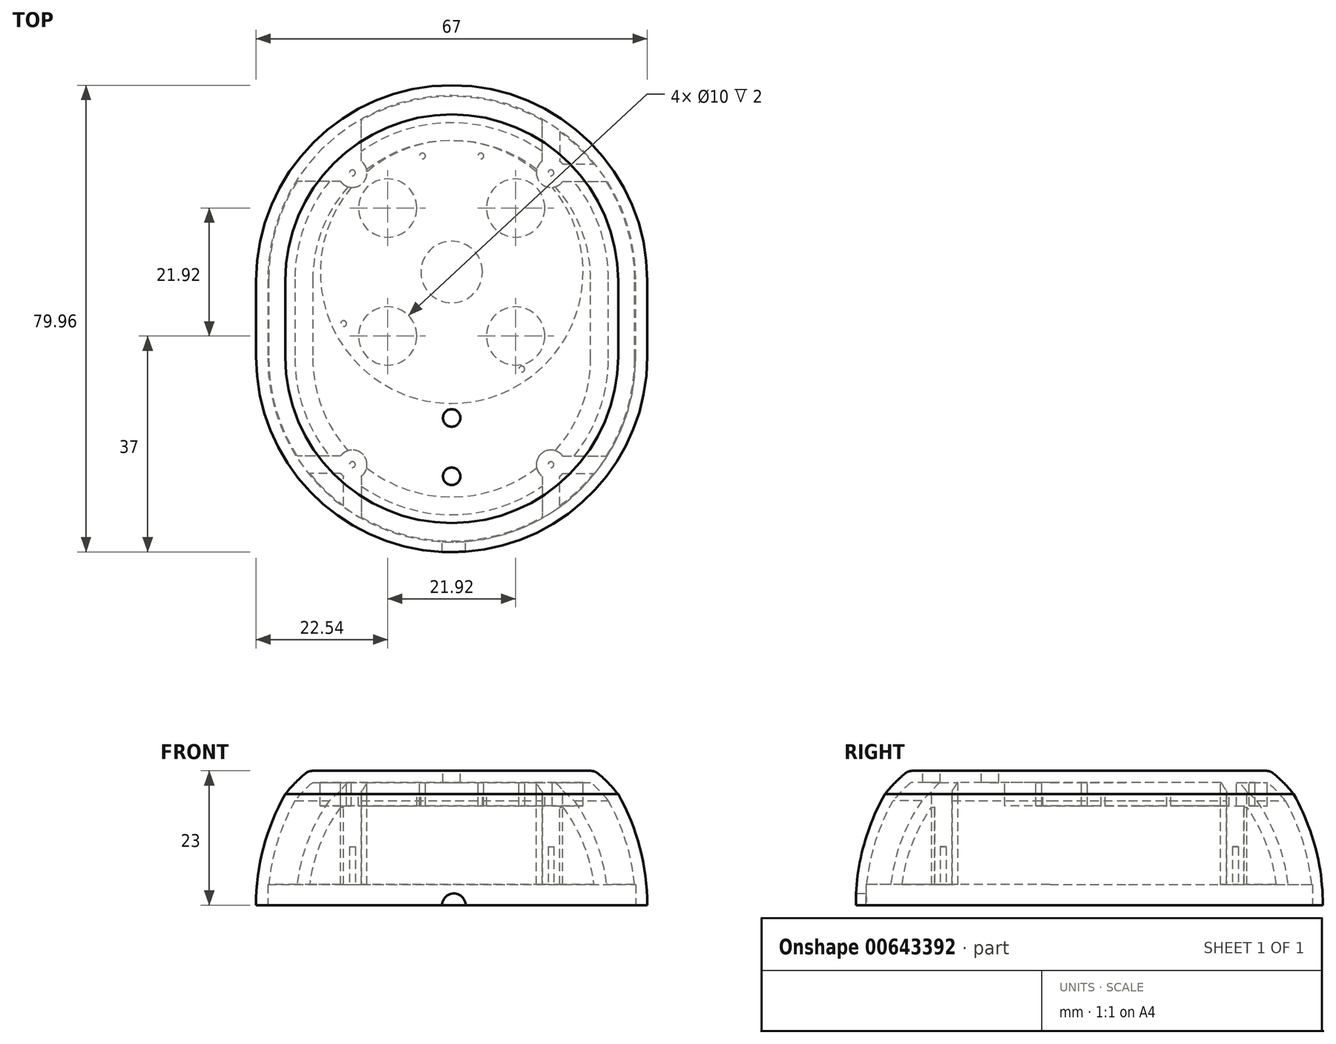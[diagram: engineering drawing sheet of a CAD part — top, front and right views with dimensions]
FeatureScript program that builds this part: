
annotation { "Feature Type Name" : "Feature", "Feature Type Description" : "" }
export const myFeature = defineFeature(function(context is Context, id is Id, definition is map)
    precondition{}
    {
        {
            var Q0;
            Q0=qCreatedBy(makeId("Front.planeOp"),FACE);
            var sketch = newSketch(context, id + "F0", { "sketchPlane" : qUnion([Q0])});
            skLineSegment(sketch, "E0", {"start": v(0, 0) * mm, "end": v(33.5, 0) * mm});
            skLineSegment(sketch, "E1", {"start": v(33.5, 0) * mm, "end": v(33.5, 19) * mm});
            skLineSegment(sketch, "E2", {"start": v(33.5, 19) * mm, "end": v(28.5, 19) * mm});
            skArc(sketch, "E3", {"start": v(33.5, 0) * mm, "mid": v(32.23, 9.82) * mm, "end": v(28.5, 19) * mm});
            skLineSegment(sketch, "E4", {"start": v(28.5, 19) * mm, "end": v(28.5, 23) * mm});
            skLineSegment(sketch, "E5", {"start": v(28.5, 23) * mm, "end": v(24.5, 23) * mm});
            skArc(sketch, "E6", {"start": v(28.5, 19) * mm, "mid": v(26.62, 21.12) * mm, "end": v(24.5, 23) * mm});
            skLineSegment(sketch, "E7", {"start": v(0, 25) * mm, "end": v(0, 0) * mm});
            skLineSegment(sketch, "E8", {"start": v(24.5, 23) * mm, "end": v(0, 23) * mm});
            skLineSegment(sketch, "E9.0", {"start": v(23.8, 21) * mm, "end": v(0, 21) * mm});
            skArc(sketch, "E9.1", {"start": v(26.83, 17.88) * mm, "mid": v(25.4, 19.52) * mm, "end": v(23.8, 21) * mm});
            skArc(sketch, "E9.2", {"start": v(31.5, 0) * mm, "mid": v(30.31, 9.24) * mm, "end": v(26.83, 17.88) * mm});
            skLineSegment(sketch, "E10", {"start": v(0, 23) * mm, "end": v(0, 32.6) * mm});
            skLineSegment(sketch, "E11", {"start": v(0, 32.6) * mm, "end": v(44.3, 32.6) * mm});
            skLineSegment(sketch, "E12", {"start": v(44.3, 32.6) * mm, "end": v(44.3, 0) * mm});
            skLineSegment(sketch, "E13", {"start": v(44.3, 0) * mm, "end": v(33.5, 0) * mm});
            skSolve(sketch);
        }
        {
            var Q0;
            {var subQ3=sQuery(id+"F0.wireOp",EDGE,"E3");Q0=makeQuery(id+"F0.imprint","IMPRINT",FACE,{"disambiguationData":[TD([[makeQuery(id+"F0.imprint","IMPRINT",EDGE,{"derivedFrom":subQ3}),1.0]])]});}
            var Q1;
            {var subQ0=sQuery(id+"F0.wireOp",EDGE,"E9.0");Q1=makeQuery(id+"F0.imprint","IMPRINT",FACE,{"disambiguationData":[TD([[makeQuery(id+"F0.imprint","IMPRINT",EDGE,{"derivedFrom":subQ0}),1.0]])]});}
            extrude(context, id + "F1", {"entities" : qUnion([Q0, Q1]), "depth" : (80 / 2 - 67 / 2) * mm, "offsetDistance" : 25 * mm});
        }
        {
            var Q0;
            Q0=makeQuery(id+"F1.opExtrude","CAP_FACE",FACE,{"disambiguationData":[OSD([sQuery(id+"F0.wireOp",EDGE,"E0"),sQuery(id+"F0.wireOp",EDGE,"E3"),sQuery(id+"F0.wireOp",EDGE,"E6"),sQuery(id+"F0.wireOp",EDGE,"E7"),sQuery(id+"F0.wireOp",EDGE,"E8")])],"isStart":false});
            var Q1;
            Q1=makeQuery(id+"F1.opExtrude","CAP_EDGE",EDGE,{"disambiguationData":[OSD([sQuery(id+"F0.wireOp",EDGE,"E7")])],"isStart":false});
            revolve(context, id + "F2", {"operationType" : NewBodyOperationType.ADD, "entities" : qUnion([Q0]), "axis" : qUnion([Q1]), "revolveType" : RevolveType.ONE_DIRECTION, "angle" : 180 * degree});
        }
        {
            var Q0;
            Q0=makeQuery(id+"F2.opRevolve","CAP_FACE",FACE,{"disambiguationData":[OSD([sQuery(id+"F0.wireOp",EDGE,"E0"),sQuery(id+"F0.wireOp",EDGE,"E3"),sQuery(id+"F0.wireOp",EDGE,"E6"),sQuery(id+"F0.wireOp",EDGE,"E7"),sQuery(id+"F0.wireOp",EDGE,"E8")])],"isStart":true});
            extrude(context, id + "F3", {"entities" : qUnion([Q0]), "operationType" : NewBodyOperationType.ADD, "depth" : (80 / 2 - 67 / 2) * mm, "offsetDistance" : 25 * mm});
        }
        {
            var Q0;
            {var subQ0=sQuery(id+"F0.wireOp",EDGE,"E9.0");Q0=makeQuery(id+"F0.imprint","IMPRINT",FACE,{"disambiguationData":[TD([[makeQuery(id+"F0.imprint","IMPRINT",EDGE,{"derivedFrom":subQ0}),1.0]])]});}
            extrude(context, id + "F4", {"entities" : qUnion([Q0]), "operationType" : NewBodyOperationType.REMOVE, "depth" : (81.5 / 2 - 68 / 2) * mm, "offsetDistance" : 25 * mm});
        }
        {
            var Q0;
            Q0=makeQuery(id+"F4.boolean.opBoolean","COPY",FACE,{"derivedFrom":makeQuery(id+"F4.opExtrude","CAP_FACE",FACE,{"disambiguationData":[OSD([sQuery(id+"F0.wireOp",EDGE,"E0"),sQuery(id+"F0.wireOp",EDGE,"E7"),sQuery(id+"F0.wireOp",EDGE,"E9.0"),sQuery(id+"F0.wireOp",EDGE,"E9.1"),sQuery(id+"F0.wireOp",EDGE,"E9.2")])],"isStart":false})});
            var Q1;
            Q1=makeQuery(id+"F4.boolean.opBoolean","COPY",EDGE,{"derivedFrom":makeQuery(id+"F4.opExtrude","CAP_EDGE",EDGE,{"disambiguationData":[OSD([sQuery(id+"F0.wireOp",EDGE,"E7")])],"isStart":false})});
            revolve(context, id + "F5", {"operationType" : NewBodyOperationType.REMOVE, "entities" : qUnion([Q0]), "axis" : qUnion([Q1]), "revolveType" : RevolveType.ONE_DIRECTION, "angle" : 180 * degree});
        }
        {
            var Q0;
            Q0=makeQuery(id+"F5.boolean.opBoolean","COPY",FACE,{"derivedFrom":makeQuery(id+"F5.opRevolve","CAP_FACE",FACE,{"disambiguationData":[OSD([sQuery(id+"F0.wireOp",EDGE,"E0"),sQuery(id+"F0.wireOp",EDGE,"E7"),sQuery(id+"F0.wireOp",EDGE,"E9.0"),sQuery(id+"F0.wireOp",EDGE,"E9.1"),sQuery(id+"F0.wireOp",EDGE,"E9.2")])],"isStart":false})});
            extrude(context, id + "F6", {"entities" : qUnion([Q0]), "operationType" : NewBodyOperationType.REMOVE, "oppositeDirection" : true, "depth" : (81.5 / 2 - 68 / 2) * mm, "offsetDistance" : 25 * mm});
        }
        {
            var Q0;
            Q0=makeQuery(id+"F1.opExtrude","SWEPT_BODY",BODY,{"disambiguationData":[OSD([sQuery(id+"F0.wireOp",EDGE,"E0"),sQuery(id+"F0.wireOp",EDGE,"E3"),sQuery(id+"F0.wireOp",EDGE,"E6"),sQuery(id+"F0.wireOp",EDGE,"E7"),sQuery(id+"F0.wireOp",EDGE,"E8")])]});
            var Q1;
            {var subQ0=sQuery(id+"F0.wireOp",EDGE,"E9.0");Q1=makeQuery(id+"F0.imprint","IMPRINT",FACE,{"disambiguationData":[TD([[makeQuery(id+"F0.imprint","IMPRINT",EDGE,{"derivedFrom":subQ0}),1.0]])]});}
            mirror(context, id + "F7", {"operationType" : NewBodyOperationType.ADD, "entities" : qUnion([Q0]), "mirrorPlane" : qUnion([Q1])});
        }
        {
            var Q0;
            {var subQ0=sQuery(id+"F0.wireOp",EDGE,"E9.0");var subQ1=makeQuery(id+"F6.boolean.opBoolean","MERGE",FACE,{"derivedFrom":[makeQuery(id+"F5.boolean.opBoolean","MERGE",FACE,{"derivedFrom":[makeQuery(id+"F4.boolean.opBoolean","COPY",FACE,{"derivedFrom":makeQuery(id+"F4.opExtrude","SWEPT_FACE",FACE,{"disambiguationData":[OSD([subQ0])]})}),makeQuery(id+"F5.opRevolve","SWEPT_FACE",FACE,{"disambiguationData":[OSD([subQ0])]})]}),makeQuery(id+"F6.opExtrude","SWEPT_FACE",FACE,{"disambiguationData":[OSD([subQ0])]})]});Q0=makeQuery(id+"F7.boolean.opBoolean","MERGE",FACE,{"derivedFrom":[subQ1,makeQuery(id+"F7.opPattern","COPY",FACE,{"derivedFrom":subQ1,"instanceName":"1"})]});}
            var sketch = newSketch(context, id + "F8", { "sketchPlane" : qUnion([Q0])});
            skLineSegment(sketch, "E14", {"start": v(0, -8) * mm, "end": v(0, 0) * mm});
            skCircle(sketch, "E15", {"center": v(0, -8) * mm, "radius": 22.5 * mm});
            skCircle(sketch, "E16", {"center": v(0, -8) * mm, "radius": 20.5 * mm});
            skCircle(sketch, "E17", {"center": v(-5, -27.88) * mm, "radius": 0.5 * mm});
            skCircle(sketch, "E18", {"center": v(5, -27.88) * mm, "radius": 0.5 * mm});
            skCircle(sketch, "E19", {"center": v(-18.5, 0.83) * mm, "radius": 0.5 * mm});
            skCircle(sketch, "E20", {"center": v(12, 8.62) * mm, "radius": 0.5 * mm});
            skLineSegment(sketch, "E21", {"start": v(-10.96, 2.96) * mm, "end": v(10.96, 2.96) * mm});
            skLineSegment(sketch, "E22", {"start": v(10.96, 2.96) * mm, "end": v(10.96, -18.96) * mm});
            skLineSegment(sketch, "E23", {"start": v(10.96, -18.96) * mm, "end": v(-10.96, -18.96) * mm});
            skLineSegment(sketch, "E24", {"start": v(-10.96, -18.96) * mm, "end": v(-10.96, 2.96) * mm});
            skLineSegment(sketch, "E25", {"start": v(10.96, -8) * mm, "end": v(0, -8) * mm});
            skCircle(sketch, "E26", {"center": v(-10.96, 2.96) * mm, "radius": 5 * mm});
            skCircle(sketch, "E27", {"center": v(-10.96, -18.96) * mm, "radius": 5 * mm});
            skCircle(sketch, "E28", {"center": v(10.96, -18.96) * mm, "radius": 5 * mm});
            skCircle(sketch, "E29", {"center": v(10.96, 2.96) * mm, "radius": 5 * mm});
            skCircle(sketch, "E30", {"center": v(0, -8) * mm, "radius": 5.28 * mm});
            skSolve(sketch);
        }
        {
            var Q0;
            {var subQ5=sQuery(id+"F8.wireOp",EDGE,"E16");var subQ7=sQuery(id+"F8.wireOp",EDGE,"E20");var subQ8=makeQuery(id+"F8.imprint","INTERSECT",VERTEX,{"disambiguationData":[OD(0.0)],"derivedFrom":[subQ5,subQ7]});Q0=makeQuery(id+"F8.imprint","IMPRINT",FACE,{"disambiguationData":[TD([[makeQuery(id+"F8.imprint","IMPRINT",EDGE,{"disambiguationData":[TD([[subQ8,1.0]])],"derivedFrom":subQ5}),1.0]])]});}
            var Q1;
            {var subQ3=sQuery(id+"F8.wireOp",EDGE,"E26");var subQ6=sQuery(id+"F8.wireOp",EDGE,"E16");var subQ10=makeQuery(id+"F8.imprint","INTERSECT",VERTEX,{"derivedFrom":[subQ6,subQ3]});Q1=makeQuery(id+"F8.imprint","IMPRINT",FACE,{"disambiguationData":[TD([[makeQuery(id+"F8.imprint","IMPRINT",EDGE,{"disambiguationData":[TD([[subQ10,-1.0]])],"derivedFrom":subQ6}),1.0]])]});}
            var Q2;
            {var subQ3=sQuery(id+"F8.wireOp",EDGE,"E22");var subQ5=makeQuery(id+"F8.imprint","IMPRINT",VERTEX,{"derivedFrom":subQ3});Q2=makeQuery(id+"F8.imprint","IMPRINT",FACE,{"disambiguationData":[TD([[makeQuery(id+"F8.imprint","IMPRINT",EDGE,{"disambiguationData":[TD([[subQ5,1.0]])],"derivedFrom":subQ3}),1.0]])]});}
            var Q3;
            {var subQ1=sQuery(id+"F8.wireOp",EDGE,"E16");var subQ11=sQuery(id+"F8.wireOp",EDGE,"E27");var subQ12=makeQuery(id+"F8.imprint","INTERSECT",VERTEX,{"derivedFrom":[subQ1,subQ11]});Q3=makeQuery(id+"F8.imprint","IMPRINT",FACE,{"disambiguationData":[TD([[makeQuery(id+"F8.imprint","IMPRINT",EDGE,{"disambiguationData":[TD([[subQ12,-1.0]])],"derivedFrom":subQ1}),1.0]])]});}
            var Q4;
            {var subQ0=sQuery(id+"F8.wireOp",EDGE,"E24");var subQ1=sQuery(id+"F8.wireOp",EDGE,"E21");var subQ2=makeQuery(id+"F8.imprint","INTERSECT",VERTEX,{"derivedFrom":[subQ1,subQ0]});Q4=makeQuery(id+"F8.imprint","IMPRINT",FACE,{"disambiguationData":[TD([[makeQuery(id+"F8.imprint","IMPRINT",EDGE,{"disambiguationData":[TD([[subQ2,-1.0]])],"derivedFrom":subQ1}),1.0]])]});}
            var Q5;
            {var subQ0=sQuery(id+"F8.wireOp",EDGE,"E24");var subQ1=sQuery(id+"F8.wireOp",EDGE,"E21");var subQ2=makeQuery(id+"F8.imprint","INTERSECT",VERTEX,{"derivedFrom":[subQ1,subQ0]});Q5=makeQuery(id+"F8.imprint","IMPRINT",FACE,{"disambiguationData":[TD([[makeQuery(id+"F8.imprint","IMPRINT",EDGE,{"disambiguationData":[TD([[subQ2,-1.0]])],"derivedFrom":subQ1}),-1.0]])]});}
            var Q6;
            {var subQ0=sQuery(id+"F8.wireOp",EDGE,"E22");var subQ1=sQuery(id+"F8.wireOp",EDGE,"E21");var subQ2=makeQuery(id+"F8.imprint","INTERSECT",VERTEX,{"derivedFrom":[subQ1,subQ0]});Q6=makeQuery(id+"F8.imprint","IMPRINT",FACE,{"disambiguationData":[TD([[makeQuery(id+"F8.imprint","IMPRINT",EDGE,{"disambiguationData":[TD([[subQ2,1.0]])],"derivedFrom":subQ1}),1.0]])]});}
            var Q7;
            {var subQ0=sQuery(id+"F8.wireOp",EDGE,"E22");var subQ1=sQuery(id+"F8.wireOp",EDGE,"E21");var subQ2=makeQuery(id+"F8.imprint","INTERSECT",VERTEX,{"derivedFrom":[subQ1,subQ0]});Q7=makeQuery(id+"F8.imprint","IMPRINT",FACE,{"disambiguationData":[TD([[makeQuery(id+"F8.imprint","IMPRINT",EDGE,{"disambiguationData":[TD([[subQ2,1.0]])],"derivedFrom":subQ1}),-1.0]])]});}
            var Q8;
            {var subQ0=sQuery(id+"F8.wireOp",EDGE,"E25");var subQ1=sQuery(id+"F8.wireOp",EDGE,"E14");var subQ2=makeQuery(id+"F8.imprint","INTERSECT",VERTEX,{"derivedFrom":[subQ1,subQ0]});Q8=makeQuery(id+"F8.imprint","IMPRINT",FACE,{"disambiguationData":[TD([[makeQuery(id+"F8.imprint","IMPRINT",EDGE,{"disambiguationData":[TD([[subQ2,-1.0]])],"derivedFrom":subQ1}),1.0]])]});}
            var Q9;
            {var subQ0=sQuery(id+"F8.wireOp",EDGE,"E25");var subQ1=sQuery(id+"F8.wireOp",EDGE,"E14");var subQ2=makeQuery(id+"F8.imprint","INTERSECT",VERTEX,{"derivedFrom":[subQ1,subQ0]});Q9=makeQuery(id+"F8.imprint","IMPRINT",FACE,{"disambiguationData":[TD([[makeQuery(id+"F8.imprint","IMPRINT",EDGE,{"disambiguationData":[TD([[subQ2,-1.0]])],"derivedFrom":subQ1}),-1.0]])]});}
            var Q10;
            {var subQ3=sQuery(id+"F8.wireOp",EDGE,"E22");var subQ19=makeQuery(id+"F8.imprint","IMPRINT",VERTEX,{"derivedFrom":subQ3});Q10=makeQuery(id+"F8.imprint","IMPRINT",FACE,{"disambiguationData":[TD([[makeQuery(id+"F8.imprint","IMPRINT",EDGE,{"disambiguationData":[TD([[subQ19,1.0]])],"derivedFrom":subQ3}),-1.0]])]});}
            var Q11;
            {var subQ0=sQuery(id+"F8.wireOp",EDGE,"E24");var subQ1=sQuery(id+"F8.wireOp",EDGE,"E23");var subQ2=makeQuery(id+"F8.imprint","INTERSECT",VERTEX,{"derivedFrom":[subQ1,subQ0]});Q11=makeQuery(id+"F8.imprint","IMPRINT",FACE,{"disambiguationData":[TD([[makeQuery(id+"F8.imprint","IMPRINT",EDGE,{"disambiguationData":[TD([[subQ2,1.0]])],"derivedFrom":subQ1}),-1.0]])]});}
            var Q12;
            {var subQ0=sQuery(id+"F8.wireOp",EDGE,"E24");var subQ1=sQuery(id+"F8.wireOp",EDGE,"E23");var subQ2=makeQuery(id+"F8.imprint","INTERSECT",VERTEX,{"derivedFrom":[subQ1,subQ0]});Q12=makeQuery(id+"F8.imprint","IMPRINT",FACE,{"disambiguationData":[TD([[makeQuery(id+"F8.imprint","IMPRINT",EDGE,{"disambiguationData":[TD([[subQ2,1.0]])],"derivedFrom":subQ1}),1.0]])]});}
            var Q13;
            {var subQ0=sQuery(id+"F8.wireOp",EDGE,"E23");var subQ1=sQuery(id+"F8.wireOp",EDGE,"E22");var subQ2=makeQuery(id+"F8.imprint","INTERSECT",VERTEX,{"derivedFrom":[subQ1,subQ0]});Q13=makeQuery(id+"F8.imprint","IMPRINT",FACE,{"disambiguationData":[TD([[makeQuery(id+"F8.imprint","IMPRINT",EDGE,{"disambiguationData":[TD([[subQ2,1.0]])],"derivedFrom":subQ1}),1.0]])]});}
            var Q14;
            {var subQ0=sQuery(id+"F8.wireOp",EDGE,"E23");var subQ1=sQuery(id+"F8.wireOp",EDGE,"E22");var subQ2=makeQuery(id+"F8.imprint","INTERSECT",VERTEX,{"derivedFrom":[subQ1,subQ0]});Q14=makeQuery(id+"F8.imprint","IMPRINT",FACE,{"disambiguationData":[TD([[makeQuery(id+"F8.imprint","IMPRINT",EDGE,{"disambiguationData":[TD([[subQ2,1.0]])],"derivedFrom":subQ1}),-1.0]])]});}
            var Q15;
            Q15=makeQuery(id+"F8.imprint","IMPRINT",FACE,{"disambiguationData":[TD([[makeQuery(id+"F8.imprint","IMPRINT",EDGE,{"derivedFrom":sQuery(id+"F8.wireOp",EDGE,"E15")}),1.0]])]});
            extrude(context, id + "F9", {"entities" : qUnion([Q0, Q1, Q2, Q3, Q4, Q5, Q6, Q7, Q8, Q9, Q10, Q11, Q12, Q13, Q14, Q15]), "operationType" : NewBodyOperationType.ADD, "depth" : 4 * mm, "offsetDistance" : 25 * mm});
        }
        {
            var Q0;
            {var subQ0=sQuery(id+"F8.wireOp",EDGE,"E24");var subQ1=sQuery(id+"F8.wireOp",EDGE,"E21");var subQ2=makeQuery(id+"F8.imprint","INTERSECT",VERTEX,{"derivedFrom":[subQ1,subQ0]});Q0=makeQuery(id+"F8.imprint","IMPRINT",FACE,{"disambiguationData":[TD([[makeQuery(id+"F8.imprint","IMPRINT",EDGE,{"disambiguationData":[TD([[subQ2,-1.0]])],"derivedFrom":subQ1}),1.0]])]});}
            var Q1;
            {var subQ0=sQuery(id+"F8.wireOp",EDGE,"E24");var subQ1=sQuery(id+"F8.wireOp",EDGE,"E21");var subQ2=makeQuery(id+"F8.imprint","INTERSECT",VERTEX,{"derivedFrom":[subQ1,subQ0]});Q1=makeQuery(id+"F8.imprint","IMPRINT",FACE,{"disambiguationData":[TD([[makeQuery(id+"F8.imprint","IMPRINT",EDGE,{"disambiguationData":[TD([[subQ2,-1.0]])],"derivedFrom":subQ1}),-1.0]])]});}
            var Q2;
            {var subQ0=sQuery(id+"F8.wireOp",EDGE,"E22");var subQ1=sQuery(id+"F8.wireOp",EDGE,"E21");var subQ2=makeQuery(id+"F8.imprint","INTERSECT",VERTEX,{"derivedFrom":[subQ1,subQ0]});Q2=makeQuery(id+"F8.imprint","IMPRINT",FACE,{"disambiguationData":[TD([[makeQuery(id+"F8.imprint","IMPRINT",EDGE,{"disambiguationData":[TD([[subQ2,1.0]])],"derivedFrom":subQ1}),1.0]])]});}
            var Q3;
            {var subQ0=sQuery(id+"F8.wireOp",EDGE,"E22");var subQ1=sQuery(id+"F8.wireOp",EDGE,"E21");var subQ2=makeQuery(id+"F8.imprint","INTERSECT",VERTEX,{"derivedFrom":[subQ1,subQ0]});Q3=makeQuery(id+"F8.imprint","IMPRINT",FACE,{"disambiguationData":[TD([[makeQuery(id+"F8.imprint","IMPRINT",EDGE,{"disambiguationData":[TD([[subQ2,1.0]])],"derivedFrom":subQ1}),-1.0]])]});}
            var Q4;
            {var subQ0=sQuery(id+"F8.wireOp",EDGE,"E23");var subQ1=sQuery(id+"F8.wireOp",EDGE,"E22");var subQ2=makeQuery(id+"F8.imprint","INTERSECT",VERTEX,{"derivedFrom":[subQ1,subQ0]});Q4=makeQuery(id+"F8.imprint","IMPRINT",FACE,{"disambiguationData":[TD([[makeQuery(id+"F8.imprint","IMPRINT",EDGE,{"disambiguationData":[TD([[subQ2,1.0]])],"derivedFrom":subQ1}),1.0]])]});}
            var Q5;
            {var subQ0=sQuery(id+"F8.wireOp",EDGE,"E23");var subQ1=sQuery(id+"F8.wireOp",EDGE,"E22");var subQ2=makeQuery(id+"F8.imprint","INTERSECT",VERTEX,{"derivedFrom":[subQ1,subQ0]});Q5=makeQuery(id+"F8.imprint","IMPRINT",FACE,{"disambiguationData":[TD([[makeQuery(id+"F8.imprint","IMPRINT",EDGE,{"disambiguationData":[TD([[subQ2,1.0]])],"derivedFrom":subQ1}),-1.0]])]});}
            var Q6;
            {var subQ0=sQuery(id+"F8.wireOp",EDGE,"E25");var subQ1=sQuery(id+"F8.wireOp",EDGE,"E14");var subQ2=makeQuery(id+"F8.imprint","INTERSECT",VERTEX,{"derivedFrom":[subQ1,subQ0]});Q6=makeQuery(id+"F8.imprint","IMPRINT",FACE,{"disambiguationData":[TD([[makeQuery(id+"F8.imprint","IMPRINT",EDGE,{"disambiguationData":[TD([[subQ2,-1.0]])],"derivedFrom":subQ1}),1.0]])]});}
            var Q7;
            {var subQ0=sQuery(id+"F8.wireOp",EDGE,"E24");var subQ1=sQuery(id+"F8.wireOp",EDGE,"E23");var subQ2=makeQuery(id+"F8.imprint","INTERSECT",VERTEX,{"derivedFrom":[subQ1,subQ0]});Q7=makeQuery(id+"F8.imprint","IMPRINT",FACE,{"disambiguationData":[TD([[makeQuery(id+"F8.imprint","IMPRINT",EDGE,{"disambiguationData":[TD([[subQ2,1.0]])],"derivedFrom":subQ1}),1.0]])]});}
            var Q8;
            {var subQ0=sQuery(id+"F8.wireOp",EDGE,"E25");var subQ1=sQuery(id+"F8.wireOp",EDGE,"E14");var subQ2=makeQuery(id+"F8.imprint","INTERSECT",VERTEX,{"derivedFrom":[subQ1,subQ0]});Q8=makeQuery(id+"F8.imprint","IMPRINT",FACE,{"disambiguationData":[TD([[makeQuery(id+"F8.imprint","IMPRINT",EDGE,{"disambiguationData":[TD([[subQ2,-1.0]])],"derivedFrom":subQ1}),-1.0]])]});}
            var Q9;
            {var subQ0=sQuery(id+"F8.wireOp",EDGE,"E24");var subQ1=sQuery(id+"F8.wireOp",EDGE,"E23");var subQ2=makeQuery(id+"F8.imprint","INTERSECT",VERTEX,{"derivedFrom":[subQ1,subQ0]});Q9=makeQuery(id+"F8.imprint","IMPRINT",FACE,{"disambiguationData":[TD([[makeQuery(id+"F8.imprint","IMPRINT",EDGE,{"disambiguationData":[TD([[subQ2,1.0]])],"derivedFrom":subQ1}),-1.0]])]});}
            extrude(context, id + "F10", {"entities" : qUnion([Q0, Q1, Q2, Q3, Q4, Q5, Q6, Q7, Q8, Q9]), "operationType" : NewBodyOperationType.REMOVE, "depth" : 4 * mm, "offsetDistance" : 25 * mm});
        }
        {
            var Q0;
            Q0=makeQuery(id+"F8.imprint","IMPRINT",FACE,{"disambiguationData":[TD([[makeQuery(id+"F8.imprint","IMPRINT",EDGE,{"derivedFrom":sQuery(id+"F8.wireOp",EDGE,"E15")}),-1.0]])]});
            var sketch = newSketch(context, id + "F11", { "sketchPlane" : qUnion([Q0])});
            skLineSegment(sketch, "E31", {"start": v(0, 0) * mm, "end": v(17, 0) * mm});
            skCircle(sketch, "E32", {"center": v(17, 25) * mm, "radius": 2.5 * mm});
            skCircle(sketch, "E33", {"center": v(-17, 25) * mm, "radius": 2.5 * mm});
            skCircle(sketch, "E34", {"center": v(-17, -25) * mm, "radius": 2.5 * mm});
            skCircle(sketch, "E35", {"center": v(17, -25) * mm, "radius": 2.5 * mm});
            skSolve(sketch);
        }
        {
            var Q0;
            Q0=qCreatedBy(makeId("Top.planeOp"),FACE);
            cPlane(context, id + "F12", {"entities" : qUnion([Q0]), "cplaneType" : CPlaneType.OFFSET, "offset" : 3.5 * mm, "width" : 150 * mm, "height" : 150 * mm});
        }
        {
            var Q0;
            Q0=qSketchRegion(id+"F11",true);
            extrude(context, id + "F13", {"entities" : qUnion([Q0]), "operationType" : NewBodyOperationType.ADD, "depth" : 21 * mm, "offsetDistance" : 25 * mm});
        }
        {
            var Q0;
            Q0=qCreatedBy(id+"F12.planeOp",FACE);
            var sketch = newSketch(context, id + "F14", { "sketchPlane" : qUnion([Q0])});
            skLineSegment(sketch, "E36.MirrorCS", {"start": v(-17, 25) * mm, "end": v(-15.5, 25) * mm});
            skLineSegment(sketch, "E37.MirrorCS", {"start": v(-17, 25) * mm, "end": v(-17, 23.5) * mm});
            skLineSegment(sketch, "E38.MirrorCS", {"start": v(-30, 26.5) * mm, "end": v(-30, 23.5) * mm});
            skLineSegment(sketch, "E39.MirrorCS", {"start": v(-15.5, 38) * mm, "end": v(-18.5, 38) * mm});
            skLineSegment(sketch, "E40.MirrorCS", {"start": v(-15.5, 25) * mm, "end": v(-15.5, 38) * mm});
            skLineSegment(sketch, "E41.MirrorCS", {"start": v(-17, 23.5) * mm, "end": v(-30, 23.5) * mm});
            skLineSegment(sketch, "E42.MirrorCS", {"start": v(-17, -25) * mm, "end": v(-17, -23.5) * mm});
            skLineSegment(sketch, "E43.MirrorCS", {"start": v(-17, -25) * mm, "end": v(-15.5, -25) * mm});
            skLineSegment(sketch, "E44.MirrorCS", {"start": v(-30, -26.5) * mm, "end": v(-30, -23.5) * mm});
            skLineSegment(sketch, "E45.MirrorCS", {"start": v(-15.5, -38) * mm, "end": v(-18.5, -38) * mm});
            skLineSegment(sketch, "E46.MirrorCS", {"start": v(-17, -23.5) * mm, "end": v(-30, -23.5) * mm});
            skLineSegment(sketch, "E47.MirrorCS", {"start": v(-15.5, -25) * mm, "end": v(-15.5, -38) * mm});
            skLineSegment(sketch, "E48", {"start": v(-18.5, -38) * mm, "end": v(-18.5, -26.5) * mm});
            skLineSegment(sketch, "E49", {"start": v(-18.5, -26.5) * mm, "end": v(-30, -26.5) * mm});
            skLineSegment(sketch, "E50", {"start": v(-30, 26.5) * mm, "end": v(-18.5, 38) * mm});
            skLineSegment(sketch, "E51.MirrorCS", {"start": v(15.5, -38) * mm, "end": v(18.5, -38) * mm});
            skLineSegment(sketch, "E52.MirrorCS", {"start": v(30, -26.5) * mm, "end": v(30, -23.5) * mm});
            skLineSegment(sketch, "E53.MirrorCS", {"start": v(17, -25) * mm, "end": v(17, -23.5) * mm});
            skLineSegment(sketch, "E54.MirrorCS", {"start": v(17, -25) * mm, "end": v(15.5, -25) * mm});
            skLineSegment(sketch, "E55.MirrorCS", {"start": v(15.5, 38) * mm, "end": v(18.5, 38) * mm});
            skLineSegment(sketch, "E56.MirrorCS", {"start": v(17, 25) * mm, "end": v(15.5, 25) * mm});
            skLineSegment(sketch, "E57.MirrorCS", {"start": v(30, 26.5) * mm, "end": v(30, 23.5) * mm});
            skLineSegment(sketch, "E58.MirrorCS", {"start": v(17, 25) * mm, "end": v(17, 23.5) * mm});
            skLineSegment(sketch, "E59.MirrorCS", {"start": v(17, 23.5) * mm, "end": v(30, 23.5) * mm});
            skLineSegment(sketch, "E60.MirrorCS", {"start": v(15.5, 25) * mm, "end": v(15.5, 38) * mm});
            skLineSegment(sketch, "E61.MirrorCS", {"start": v(15.5, -25) * mm, "end": v(15.5, -38) * mm});
            skLineSegment(sketch, "E62.MirrorCS", {"start": v(18.5, -38) * mm, "end": v(18.5, -26.5) * mm});
            skLineSegment(sketch, "E63.MirrorCS", {"start": v(17, -23.5) * mm, "end": v(30, -23.5) * mm});
            skLineSegment(sketch, "E64.MirrorCS", {"start": v(18.5, -26.5) * mm, "end": v(30, -26.5) * mm});
            skLineSegment(sketch, "E65", {"start": v(18.5, 38) * mm, "end": v(18.5, 26.5) * mm});
            skLineSegment(sketch, "E66", {"start": v(18.5, 26.5) * mm, "end": v(30, 26.5) * mm});
            skSolve(sketch);
        }
        {
            var Q0;
            {var subQ0=sQuery(id+"F0.wireOp",EDGE,"E0");var subQ1=makeQuery(id+"F3.boolean.opBoolean","MERGE",FACE,{"derivedFrom":[makeQuery(id+"F2.boolean.opBoolean","MERGE",FACE,{"derivedFrom":[makeQuery(id+"F1.opExtrude","SWEPT_FACE",FACE,{"disambiguationData":[OSD([subQ0])]}),makeQuery(id+"F2.opRevolve","SWEPT_FACE",FACE,{"disambiguationData":[OSD([subQ0])]})]}),makeQuery(id+"F3.opExtrude","SWEPT_FACE",FACE,{"disambiguationData":[OSD([subQ0])]})]});Q0=makeQuery(id+"F7.boolean.opBoolean","MERGE",FACE,{"derivedFrom":[subQ1,makeQuery(id+"F7.opPattern","COPY",FACE,{"derivedFrom":subQ1,"instanceName":"1"})]});}
            var sketch = newSketch(context, id + "F15", { "sketchPlane" : qUnion([Q0])});
            skLineSegment(sketch, "E67", {"start": v(-17, 25) * mm, "end": v(-17, 23.5) * mm});
            skLineSegment(sketch, "E68", {"start": v(-17, 23.5) * mm, "end": v(-30, 23.5) * mm});
            skLineSegment(sketch, "E69", {"start": v(-17, 25) * mm, "end": v(-15.5, 25) * mm});
            skLineSegment(sketch, "E70", {"start": v(-15.5, 25) * mm, "end": v(-15.5, 38) * mm});
            skLineSegment(sketch, "E71", {"start": v(-15.5, 38) * mm, "end": v(-18.5, 38) * mm});
            skLineSegment(sketch, "E72", {"start": v(-18.5, 38) * mm, "end": v(-18.5, 26.5) * mm});
            skLineSegment(sketch, "E73", {"start": v(-18.5, 26.5) * mm, "end": v(-30, 26.5) * mm});
            skLineSegment(sketch, "E74", {"start": v(-30, 26.5) * mm, "end": v(-30, 23.5) * mm});
            skLineSegment(sketch, "E75.MirrorCS", {"start": v(30, 26.5) * mm, "end": v(30, 23.5) * mm});
            skLineSegment(sketch, "E76.MirrorCS", {"start": v(18.5, 26.5) * mm, "end": v(30, 26.5) * mm});
            skLineSegment(sketch, "E77.MirrorCS", {"start": v(18.5, 38) * mm, "end": v(18.5, 26.5) * mm});
            skLineSegment(sketch, "E78.MirrorCS", {"start": v(15.5, 38) * mm, "end": v(18.5, 38) * mm});
            skLineSegment(sketch, "E79.MirrorCS", {"start": v(17, 25) * mm, "end": v(17, 23.5) * mm});
            skLineSegment(sketch, "E80.MirrorCS", {"start": v(15.5, 25) * mm, "end": v(15.5, 38) * mm});
            skLineSegment(sketch, "E81.MirrorCS", {"start": v(17, 23.5) * mm, "end": v(30, 23.5) * mm});
            skLineSegment(sketch, "E82.MirrorCS", {"start": v(17, 25) * mm, "end": v(15.5, 25) * mm});
            skLineSegment(sketch, "E83.MirrorCS", {"start": v(17, -25) * mm, "end": v(17, -23.5) * mm});
            skLineSegment(sketch, "E84.MirrorCS", {"start": v(17, -25) * mm, "end": v(15.5, -25) * mm});
            skLineSegment(sketch, "E85.MirrorCS", {"start": v(30, -26.5) * mm, "end": v(30, -23.5) * mm});
            skLineSegment(sketch, "E86.MirrorCS", {"start": v(15.5, -38) * mm, "end": v(18.5, -38) * mm});
            skLineSegment(sketch, "E87.MirrorCS", {"start": v(-17, -25) * mm, "end": v(-17, -23.5) * mm});
            skLineSegment(sketch, "E88.MirrorCS", {"start": v(-17, -25) * mm, "end": v(-15.5, -25) * mm});
            skLineSegment(sketch, "E89.MirrorCS", {"start": v(-30, -26.5) * mm, "end": v(-30, -23.5) * mm});
            skLineSegment(sketch, "E90.MirrorCS", {"start": v(-15.5, -38) * mm, "end": v(-18.5, -38) * mm});
            skLineSegment(sketch, "E91.MirrorCS", {"start": v(15.5, -25) * mm, "end": v(15.5, -38) * mm});
            skLineSegment(sketch, "E92.MirrorCS", {"start": v(18.5, -26.5) * mm, "end": v(30, -26.5) * mm});
            skLineSegment(sketch, "E93.MirrorCS", {"start": v(17, -23.5) * mm, "end": v(30, -23.5) * mm});
            skLineSegment(sketch, "E94.MirrorCS", {"start": v(18.5, -38) * mm, "end": v(18.5, -26.5) * mm});
            skLineSegment(sketch, "E95.MirrorCS", {"start": v(-17, -23.5) * mm, "end": v(-30, -23.5) * mm});
            skLineSegment(sketch, "E96.MirrorCS", {"start": v(-15.5, -25) * mm, "end": v(-15.5, -38) * mm});
            skLineSegment(sketch, "E97", {"start": v(-30, -26.5) * mm, "end": v(-18.5, -38) * mm});
            skSolve(sketch);
        }
        {
            var Q0;
            Q0=qSketchRegion(id+"F14",true);
            extrude(context, id + "F16", {"entities" : qUnion([Q0]), "operationType" : NewBodyOperationType.ADD, "depth" : 25 * mm, "offsetDistance" : 25 * mm});
        }
        {
            var Q0;
            {var subQ0=sQuery(id+"F0.wireOp",EDGE,"E0");var subQ1=makeQuery(id+"F3.boolean.opBoolean","MERGE",FACE,{"derivedFrom":[makeQuery(id+"F2.boolean.opBoolean","MERGE",FACE,{"derivedFrom":[makeQuery(id+"F1.opExtrude","SWEPT_FACE",FACE,{"disambiguationData":[OSD([subQ0])]}),makeQuery(id+"F2.opRevolve","SWEPT_FACE",FACE,{"disambiguationData":[OSD([subQ0])]})]}),makeQuery(id+"F3.opExtrude","SWEPT_FACE",FACE,{"disambiguationData":[OSD([subQ0])]})]});Q0=makeQuery(id+"F16.boolean.opBoolean","MERGE",FACE,{"derivedFrom":[makeQuery(id+"F7.boolean.opBoolean","MERGE",FACE,{"derivedFrom":[subQ1,makeQuery(id+"F7.opPattern","COPY",FACE,{"derivedFrom":subQ1,"instanceName":"1"})]}),makeQuery(id+"F13.opExtrude","CAP_FACE",FACE,{"disambiguationData":[OSD([sQuery(id+"F11.wireOp",EDGE,"E32")])],"isStart":false}),makeQuery(id+"F13.opExtrude","CAP_FACE",FACE,{"disambiguationData":[OSD([sQuery(id+"F11.wireOp",EDGE,"E33")])],"isStart":false}),makeQuery(id+"F13.opExtrude","CAP_FACE",FACE,{"disambiguationData":[OSD([sQuery(id+"F11.wireOp",EDGE,"E34")])],"isStart":false}),makeQuery(id+"F13.opExtrude","CAP_FACE",FACE,{"disambiguationData":[OSD([sQuery(id+"F11.wireOp",EDGE,"E35")])],"isStart":false}),makeQuery(id+"F16.opExtrude","CAP_FACE",FACE,{"disambiguationData":[OSD([sQuery(id+"F15.wireOp",EDGE,"E69"),sQuery(id+"F15.wireOp",EDGE,"E67"),sQuery(id+"F15.wireOp",EDGE,"E72"),sQuery(id+"F15.wireOp",EDGE,"E73"),sQuery(id+"F15.wireOp",EDGE,"E74"),sQuery(id+"F15.wireOp",EDGE,"E71"),sQuery(id+"F15.wireOp",EDGE,"E70"),sQuery(id+"F15.wireOp",EDGE,"E68")])],"isStart":true}),makeQuery(id+"F16.opExtrude","CAP_FACE",FACE,{"disambiguationData":[OSD([sQuery(id+"F15.wireOp",EDGE,"E82.MirrorCS"),sQuery(id+"F15.wireOp",EDGE,"E79.MirrorCS"),sQuery(id+"F15.wireOp",EDGE,"E78.MirrorCS"),sQuery(id+"F15.wireOp",EDGE,"E81.MirrorCS"),sQuery(id+"F15.wireOp",EDGE,"E75.MirrorCS"),sQuery(id+"F15.wireOp",EDGE,"E80.MirrorCS"),sQuery(id+"F15.wireOp",EDGE,"E76.MirrorCS"),sQuery(id+"F15.wireOp",EDGE,"E77.MirrorCS")])],"isStart":true}),makeQuery(id+"F16.opExtrude","CAP_FACE",FACE,{"disambiguationData":[OSD([sQuery(id+"F15.wireOp",EDGE,"E83.MirrorCS"),sQuery(id+"F15.wireOp",EDGE,"E84.MirrorCS"),sQuery(id+"F15.wireOp",EDGE,"E85.MirrorCS"),sQuery(id+"F15.wireOp",EDGE,"E86.MirrorCS"),sQuery(id+"F15.wireOp",EDGE,"E94.MirrorCS"),sQuery(id+"F15.wireOp",EDGE,"E92.MirrorCS"),sQuery(id+"F15.wireOp",EDGE,"E93.MirrorCS"),sQuery(id+"F15.wireOp",EDGE,"E91.MirrorCS")])],"isStart":true}),makeQuery(id+"F16.opExtrude","CAP_FACE",FACE,{"disambiguationData":[OSD([sQuery(id+"F15.wireOp",EDGE,"E87.MirrorCS"),sQuery(id+"F15.wireOp",EDGE,"E88.MirrorCS"),sQuery(id+"F15.wireOp",EDGE,"E89.MirrorCS"),sQuery(id+"F15.wireOp",EDGE,"E90.MirrorCS"),sQuery(id+"F15.wireOp",EDGE,"E95.MirrorCS"),sQuery(id+"F15.wireOp",EDGE,"E96.MirrorCS"),sQuery(id+"F15.wireOp",EDGE,"E97")])],"isStart":true})]});}
            var sketch = newSketch(context, id + "F17", { "sketchPlane" : qUnion([Q0])});
            skCircle(sketch, "E98", {"center": v(17, 25) * mm, "radius": 0.5 * mm});
            skCircle(sketch, "E99", {"center": v(-17, 25) * mm, "radius": 0.5 * mm});
            skCircle(sketch, "E100", {"center": v(-17, -25) * mm, "radius": 0.5 * mm});
            skCircle(sketch, "E101", {"center": v(17, -25) * mm, "radius": 0.5 * mm});
            skSolve(sketch);
        }
        {
            var Q0;
            Q0=qSketchRegion(id+"F17",true);
            extrude(context, id + "F18", {"entities" : qUnion([Q0]), "operationType" : NewBodyOperationType.REMOVE, "oppositeDirection" : true, "depth" : 10 * mm, "offsetDistance" : 25 * mm});
        }
        {
            var Q0;
            Q0=qCreatedBy(makeId("Front.planeOp"),FACE);
            var sketch = newSketch(context, id + "F19", { "sketchPlane" : qUnion([Q0])});
            skCircle(sketch, "E102", {"center": v(0.38, 0) * mm, "radius": 2 * mm});
            skSolve(sketch);
        }
        {
            var Q0;
            Q0=qSketchRegion(id+"F19",true);
            extrude(context, id + "F20", {"entities" : qUnion([Q0]), "operationType" : NewBodyOperationType.REMOVE, "depth" : 45 * mm, "offsetDistance" : 25 * mm});
        }
        {
            var Q0;
            Q0=makeQuery(id+"F0.imprint","IMPRINT",FACE,{"disambiguationData":[TD([[makeQuery(id+"F0.imprint","IMPRINT",EDGE,{"derivedFrom":sQuery(id+"F0.wireOp",EDGE,"E1")}),-1.0]])]});
            var Q1;
            Q1=makeQuery(id+"F0.imprint","IMPRINT",FACE,{"disambiguationData":[TD([[makeQuery(id+"F0.imprint","IMPRINT",EDGE,{"derivedFrom":sQuery(id+"F0.wireOp",EDGE,"E4")}),1.0]])]});
            var Q2;
            Q2=makeQuery(id+"F0.imprint","IMPRINT",FACE,{"disambiguationData":[TD([[makeQuery(id+"F0.imprint","IMPRINT",EDGE,{"derivedFrom":sQuery(id+"F0.wireOp",EDGE,"E1")}),1.0]])]});
            extrude(context, id + "F21", {"entities" : qUnion([Q0, Q1, Q2]), "operationType" : NewBodyOperationType.ADD, "depth" : (13 / 2) * mm, "offsetDistance" : 25 * mm});
        }
        {
            var Q0;
            Q0=qSketchRegion(id+"F8",true);
            var Q1;
            {var subQ0=sQuery(id+"F8.wireOp",EDGE,"E24");var subQ1=sQuery(id+"F8.wireOp",EDGE,"E21");var subQ2=makeQuery(id+"F8.imprint","INTERSECT",VERTEX,{"derivedFrom":[subQ1,subQ0]});Q1=makeQuery(id+"F8.imprint","IMPRINT",FACE,{"disambiguationData":[TD([[makeQuery(id+"F8.imprint","IMPRINT",EDGE,{"disambiguationData":[TD([[subQ2,-1.0]])],"derivedFrom":subQ1}),1.0]])]});}
            var Q2;
            {var subQ0=sQuery(id+"F8.wireOp",EDGE,"E24");var subQ1=sQuery(id+"F8.wireOp",EDGE,"E21");var subQ2=makeQuery(id+"F8.imprint","INTERSECT",VERTEX,{"derivedFrom":[subQ1,subQ0]});Q2=makeQuery(id+"F8.imprint","IMPRINT",FACE,{"disambiguationData":[TD([[makeQuery(id+"F8.imprint","IMPRINT",EDGE,{"disambiguationData":[TD([[subQ2,-1.0]])],"derivedFrom":subQ1}),-1.0]])]});}
            var Q3;
            {var subQ0=sQuery(id+"F8.wireOp",EDGE,"E22");var subQ1=sQuery(id+"F8.wireOp",EDGE,"E21");var subQ2=makeQuery(id+"F8.imprint","INTERSECT",VERTEX,{"derivedFrom":[subQ1,subQ0]});Q3=makeQuery(id+"F8.imprint","IMPRINT",FACE,{"disambiguationData":[TD([[makeQuery(id+"F8.imprint","IMPRINT",EDGE,{"disambiguationData":[TD([[subQ2,1.0]])],"derivedFrom":subQ1}),1.0]])]});}
            var Q4;
            {var subQ0=sQuery(id+"F8.wireOp",EDGE,"E22");var subQ1=sQuery(id+"F8.wireOp",EDGE,"E21");var subQ2=makeQuery(id+"F8.imprint","INTERSECT",VERTEX,{"derivedFrom":[subQ1,subQ0]});Q4=makeQuery(id+"F8.imprint","IMPRINT",FACE,{"disambiguationData":[TD([[makeQuery(id+"F8.imprint","IMPRINT",EDGE,{"disambiguationData":[TD([[subQ2,1.0]])],"derivedFrom":subQ1}),-1.0]])]});}
            var Q5;
            {var subQ0=sQuery(id+"F8.wireOp",EDGE,"E23");var subQ1=sQuery(id+"F8.wireOp",EDGE,"E22");var subQ2=makeQuery(id+"F8.imprint","INTERSECT",VERTEX,{"derivedFrom":[subQ1,subQ0]});Q5=makeQuery(id+"F8.imprint","IMPRINT",FACE,{"disambiguationData":[TD([[makeQuery(id+"F8.imprint","IMPRINT",EDGE,{"disambiguationData":[TD([[subQ2,1.0]])],"derivedFrom":subQ1}),1.0]])]});}
            var Q6;
            {var subQ0=sQuery(id+"F8.wireOp",EDGE,"E23");var subQ1=sQuery(id+"F8.wireOp",EDGE,"E22");var subQ2=makeQuery(id+"F8.imprint","INTERSECT",VERTEX,{"derivedFrom":[subQ1,subQ0]});Q6=makeQuery(id+"F8.imprint","IMPRINT",FACE,{"disambiguationData":[TD([[makeQuery(id+"F8.imprint","IMPRINT",EDGE,{"disambiguationData":[TD([[subQ2,1.0]])],"derivedFrom":subQ1}),-1.0]])]});}
            var Q7;
            {var subQ0=sQuery(id+"F8.wireOp",EDGE,"E24");var subQ1=sQuery(id+"F8.wireOp",EDGE,"E23");var subQ2=makeQuery(id+"F8.imprint","INTERSECT",VERTEX,{"derivedFrom":[subQ1,subQ0]});Q7=makeQuery(id+"F8.imprint","IMPRINT",FACE,{"disambiguationData":[TD([[makeQuery(id+"F8.imprint","IMPRINT",EDGE,{"disambiguationData":[TD([[subQ2,1.0]])],"derivedFrom":subQ1}),1.0]])]});}
            var Q8;
            {var subQ0=sQuery(id+"F8.wireOp",EDGE,"E24");var subQ1=sQuery(id+"F8.wireOp",EDGE,"E23");var subQ2=makeQuery(id+"F8.imprint","INTERSECT",VERTEX,{"derivedFrom":[subQ1,subQ0]});Q8=makeQuery(id+"F8.imprint","IMPRINT",FACE,{"disambiguationData":[TD([[makeQuery(id+"F8.imprint","IMPRINT",EDGE,{"disambiguationData":[TD([[subQ2,1.0]])],"derivedFrom":subQ1}),-1.0]])]});}
            var Q9;
            {var subQ0=sQuery(id+"F8.wireOp",EDGE,"E25");var subQ1=sQuery(id+"F8.wireOp",EDGE,"E14");var subQ2=makeQuery(id+"F8.imprint","INTERSECT",VERTEX,{"derivedFrom":[subQ1,subQ0]});Q9=makeQuery(id+"F8.imprint","IMPRINT",FACE,{"disambiguationData":[TD([[makeQuery(id+"F8.imprint","IMPRINT",EDGE,{"disambiguationData":[TD([[subQ2,-1.0]])],"derivedFrom":subQ1}),1.0]])]});}
            var Q10;
            {var subQ0=sQuery(id+"F8.wireOp",EDGE,"E25");var subQ1=sQuery(id+"F8.wireOp",EDGE,"E14");var subQ2=makeQuery(id+"F8.imprint","INTERSECT",VERTEX,{"derivedFrom":[subQ1,subQ0]});Q10=makeQuery(id+"F8.imprint","IMPRINT",FACE,{"disambiguationData":[TD([[makeQuery(id+"F8.imprint","IMPRINT",EDGE,{"disambiguationData":[TD([[subQ2,-1.0]])],"derivedFrom":subQ1}),-1.0]])]});}
            extrude(context, id + "F22", {"entities" : qUnion([Q0, Q1, Q2, Q3, Q4, Q5, Q6, Q7, Q8, Q9, Q10]), "operationType" : NewBodyOperationType.ADD, "depth" : 2 * mm, "offsetDistance" : 25 * mm});
        }
        {
            var Q0;
            Q0=makeQuery(id+"F9.opExtrude","CAP_FACE",FACE,{"disambiguationData":[OSD([sQuery(id+"F8.wireOp",EDGE,"E15"),sQuery(id+"F8.wireOp",EDGE,"E17"),sQuery(id+"F8.wireOp",EDGE,"E18"),sQuery(id+"F8.wireOp",EDGE,"E19"),sQuery(id+"F8.wireOp",EDGE,"E20")])],"isStart":false});
            var sketch = newSketch(context, id + "F23", { "sketchPlane" : qUnion([Q0])});
            skLineSegment(sketch, "E103", {"start": v(0, 0) * mm, "end": v(0, -8) * mm});
            skLineSegment(sketch, "E104", {"start": v(0, -8) * mm, "end": v(-22, -8) * mm});
            skLineSegment(sketch, "E105", {"start": v(-22, -8) * mm, "end": v(-22, -1.75) * mm});
            skLineSegment(sketch, "E106", {"start": v(-22, -1.75) * mm, "end": v(-32, -1.75) * mm});
            skLineSegment(sketch, "E107", {"start": v(-32, -1.75) * mm, "end": v(-32, -14.25) * mm});
            skLineSegment(sketch, "E108", {"start": v(-32, -14.25) * mm, "end": v(-22, -14.25) * mm});
            skLineSegment(sketch, "E109", {"start": v(-22, -14.25) * mm, "end": v(-22, -8) * mm});
            skSolve(sketch);
        }
        {
            var Q0;
            Q0=makeQuery(id+"F21.opExtrude","CAP_FACE",FACE,{"disambiguationData":[OSD([sQuery(id+"F0.wireOp",EDGE,"E3"),sQuery(id+"F0.wireOp",EDGE,"E6"),sQuery(id+"F0.wireOp",EDGE,"E8"),sQuery(id+"F0.wireOp",EDGE,"E10"),sQuery(id+"F0.wireOp",EDGE,"E11"),sQuery(id+"F0.wireOp",EDGE,"E12"),sQuery(id+"F0.wireOp",EDGE,"E13")])],"isStart":false});
            var Q1;
            Q1=makeQuery(id+"F21.opExtrude","CAP_EDGE",EDGE,{"disambiguationData":[OSD([sQuery(id+"F0.wireOp",EDGE,"E10")])],"isStart":false});
            revolve(context, id + "F24", {"operationType" : NewBodyOperationType.REMOVE, "entities" : qUnion([Q0]), "axis" : qUnion([Q1]), "revolveType" : RevolveType.ONE_DIRECTION, "oppositeDirection" : true, "angle" : 180 * degree});
        }
        {
            var Q0;
            Q0=makeQuery(id+"F0.imprint","IMPRINT",FACE,{"disambiguationData":[TD([[makeQuery(id+"F0.imprint","IMPRINT",EDGE,{"derivedFrom":sQuery(id+"F0.wireOp",EDGE,"E1")}),-1.0]])]});
            var Q1;
            Q1=makeQuery(id+"F0.imprint","IMPRINT",FACE,{"disambiguationData":[TD([[makeQuery(id+"F0.imprint","IMPRINT",EDGE,{"derivedFrom":sQuery(id+"F0.wireOp",EDGE,"E4")}),1.0]])]});
            var Q2;
            Q2=makeQuery(id+"F0.imprint","IMPRINT",FACE,{"disambiguationData":[TD([[makeQuery(id+"F0.imprint","IMPRINT",EDGE,{"derivedFrom":sQuery(id+"F0.wireOp",EDGE,"E1")}),1.0]])]});
            extrude(context, id + "F25", {"entities" : qUnion([Q0, Q1, Q2]), "operationType" : NewBodyOperationType.ADD, "depth" : (-13 / 2) * mm, "offsetDistance" : 25 * mm});
        }
        {
            var Q0;
            Q0=makeQuery(id+"F25.opExtrude","CAP_FACE",FACE,{"disambiguationData":[OSD([sQuery(id+"F0.wireOp",EDGE,"E3"),sQuery(id+"F0.wireOp",EDGE,"E6"),sQuery(id+"F0.wireOp",EDGE,"E8"),sQuery(id+"F0.wireOp",EDGE,"E10"),sQuery(id+"F0.wireOp",EDGE,"E11"),sQuery(id+"F0.wireOp",EDGE,"E12"),sQuery(id+"F0.wireOp",EDGE,"E13")])],"isStart":false});
            var Q1;
            Q1=makeQuery(id+"F25.opExtrude","CAP_EDGE",EDGE,{"disambiguationData":[OSD([sQuery(id+"F0.wireOp",EDGE,"E10")])],"isStart":false});
            revolve(context, id + "F26", {"operationType" : NewBodyOperationType.REMOVE, "entities" : qUnion([Q0]), "axis" : qUnion([Q1]), "revolveType" : RevolveType.ONE_DIRECTION, "angle" : 180 * degree});
        }
        {
            var Q0;
            Q0=makeQuery(id+"F25.opExtrude","CAP_FACE",FACE,{"disambiguationData":[OSD([sQuery(id+"F0.wireOp",EDGE,"E3"),sQuery(id+"F0.wireOp",EDGE,"E6"),sQuery(id+"F0.wireOp",EDGE,"E8"),sQuery(id+"F0.wireOp",EDGE,"E10"),sQuery(id+"F0.wireOp",EDGE,"E11"),sQuery(id+"F0.wireOp",EDGE,"E12"),sQuery(id+"F0.wireOp",EDGE,"E13")])],"isStart":false});
            extrude(context, id + "F27", {"entities" : qUnion([Q0]), "operationType" : NewBodyOperationType.REMOVE, "oppositeDirection" : true, "depth" : 13 * mm, "offsetDistance" : 25 * mm});
        }
        {
            var Q0;
            {var subQ0=sQuery(id+"F0.wireOp",EDGE,"E8");var subQ1=makeQuery(id+"F3.opExtrude","SWEPT_FACE",FACE,{"disambiguationData":[OSD([subQ0])]});var subQ2=makeQuery(id+"F2.opRevolve","SWEPT_FACE",FACE,{"disambiguationData":[OSD([subQ0])]});var subQ3=sQuery(id+"F0.wireOp",EDGE,"E6");var subQ4=makeQuery(id+"F1.opExtrude","SWEPT_FACE",FACE,{"disambiguationData":[OSD([subQ0])]});var subQ5=makeQuery(id+"F3.boolean.opBoolean","MERGE",FACE,{"derivedFrom":[makeQuery(id+"F2.boolean.opBoolean","MERGE",FACE,{"derivedFrom":[subQ4,subQ2]}),subQ1]});var subQ6=makeQuery(id+"F7.opPattern","COPY",FACE,{"derivedFrom":subQ5,"instanceName":"1"});Q0=makeQuery(id+"FmzSy8yVIfiXDki_2.boolean.opBoolean","MERGE",FACE,{"derivedFrom":[makeQuery(id+"F27.boolean.opBoolean","MERGE",FACE,{"derivedFrom":[makeQuery(id+"F26.boolean.opBoolean","MERGE",FACE,{"derivedFrom":[makeQuery(id+"F24.boolean.opBoolean","MERGE",FACE,{"derivedFrom":[makeQuery(id+"F7.boolean.opBoolean","MERGE",FACE,{"derivedFrom":[subQ5,subQ6]}),makeQuery(id+"F24.opRevolve","SWEPT_FACE",FACE,{"disambiguationData":[OSD([subQ0]),TDD([makeQuery(id+"FjMn7NgZJog52uS_2.boolean.opBoolean","SPLIT",EDGE,{"disambiguationData":[TD([makeQuery(id+"F2.opRevolve","SWEPT_FACE",FACE,{"disambiguationData":[OSD([subQ3])]})])],"derivedFrom":makeQuery(id+"F21.opExtrude","CAP_EDGE",EDGE,{"disambiguationData":[OSD([subQ0])],"isStart":false})})])]})]}),makeQuery(id+"F26.opRevolve","SWEPT_FACE",FACE,{"disambiguationData":[OSD([subQ0])]})]}),makeQuery(id+"F27.opExtrude","SWEPT_FACE",FACE,{"disambiguationData":[OSD([subQ0])]})]}),makeQuery(id+"FmzSy8yVIfiXDki_2.opExtrude","SWEPT_FACE",FACE,{"disambiguationData":[OSD([subQ0,sQuery(id+"F23.wireOp",EDGE,"E106")])]})]});}
            var sketch = newSketch(context, id + "F28", { "sketchPlane" : qUnion([Q0])});
            skLineSegment(sketch, "E110", {"start": v(0, 0) * mm, "end": v(0, -17) * mm});
            skLineSegment(sketch, "E111", {"start": v(0, -17) * mm, "end": v(0, -27) * mm});
            skCircle(sketch, "E112", {"center": v(0, -17) * mm, "radius": 1.5 * mm});
            skCircle(sketch, "E113", {"center": v(0, -27) * mm, "radius": 1.5 * mm});
            skSolve(sketch);
        }
        {
            var Q0;
            Q0=qSketchRegion(id+"F28",true);
            extrude(context, id + "F29", {"entities" : qUnion([Q0]), "operationType" : NewBodyOperationType.REMOVE, "oppositeDirection" : true, "depth" : 25 * mm, "offsetDistance" : 25 * mm});
        }
        {
            var Q0;
            {var subQ7=sQuery(id+"F15.wireOp",EDGE,"E69");Q0=makeQuery(id+"F15.imprint","IMPRINT",FACE,{"disambiguationData":[TD([[makeQuery(id+"F15.imprint","IMPRINT",EDGE,{"derivedFrom":subQ7}),1.0]])]});}
            var Q1;
            {var subQ29=sQuery(id+"F15.wireOp",EDGE,"E69");Q1=makeQuery(id+"F15.imprint","IMPRINT",FACE,{"disambiguationData":[TD([[makeQuery(id+"F15.imprint","IMPRINT",EDGE,{"derivedFrom":subQ29}),-1.0]])]});}
            var Q2;
            {var subQ1=sQuery(id+"F15.wireOp",EDGE,"E82.MirrorCS");Q2=makeQuery(id+"F15.imprint","IMPRINT",FACE,{"disambiguationData":[TD([[makeQuery(id+"F15.imprint","IMPRINT",EDGE,{"derivedFrom":subQ1}),-1.0]])]});}
            var Q3;
            {var subQ9=sQuery(id+"F15.wireOp",EDGE,"E83.MirrorCS");Q3=makeQuery(id+"F15.imprint","IMPRINT",FACE,{"disambiguationData":[TD([[makeQuery(id+"F15.imprint","IMPRINT",EDGE,{"derivedFrom":subQ9}),-1.0]])]});}
            var Q4;
            {var subQ1=sQuery(id+"F15.wireOp",EDGE,"E87.MirrorCS");Q4=makeQuery(id+"F15.imprint","IMPRINT",FACE,{"disambiguationData":[TD([[makeQuery(id+"F15.imprint","IMPRINT",EDGE,{"derivedFrom":subQ1}),1.0]])]});}
            var Q5;
            {var subQ0=sQuery(id+"F15.wireOp",EDGE,"E92.MirrorCS");var subQ1=sQuery(id+"F15.wireOp",EDGE,"E94.MirrorCS");var subQ2=makeQuery(id+"F15.imprint","INTERSECT",VERTEX,{"derivedFrom":[subQ1,subQ0]});Q5=makeQuery(id+"F15.imprint","IMPRINT",FACE,{"disambiguationData":[TD([[makeQuery(id+"F15.imprint","IMPRINT",EDGE,{"disambiguationData":[TD([[subQ2,1.0]])],"derivedFrom":subQ1}),-1.0]])]});}
            var Q6;
            {var subQ0=sQuery(id+"F15.wireOp",EDGE,"E77.MirrorCS");var subQ1=sQuery(id+"F15.wireOp",EDGE,"E76.MirrorCS");var subQ2=makeQuery(id+"F15.imprint","INTERSECT",VERTEX,{"derivedFrom":[subQ1,subQ0]});Q6=makeQuery(id+"F15.imprint","IMPRINT",FACE,{"disambiguationData":[TD([[makeQuery(id+"F15.imprint","IMPRINT",EDGE,{"disambiguationData":[TD([[subQ2,-1.0]])],"derivedFrom":subQ1}),1.0]])]});}
            var Q7;
            {var subQ0=sQuery(id+"F15.wireOp",EDGE,"E73");var subQ1=sQuery(id+"F15.wireOp",EDGE,"E72");var subQ2=makeQuery(id+"F15.imprint","INTERSECT",VERTEX,{"derivedFrom":[subQ1,subQ0]});Q7=makeQuery(id+"F15.imprint","IMPRINT",FACE,{"disambiguationData":[TD([[makeQuery(id+"F15.imprint","IMPRINT",EDGE,{"disambiguationData":[TD([[subQ2,1.0]])],"derivedFrom":subQ1}),-1.0]])]});}
            extrude(context, id + "F30", {"entities" : qUnion([Q0, Q1, Q2, Q3, Q4, Q5, Q6, Q7]), "operationType" : NewBodyOperationType.REMOVE, "oppositeDirection" : true, "depth" : 3.5 * mm, "offsetDistance" : 25 * mm});
        }
        {
            var Q0;
            {var subQ0=sQuery(id+"F0.wireOp",EDGE,"E8");var subQ1=sQuery(id+"F0.wireOp",EDGE,"E6");var subQ2=sQuery(id+"F0.wireOp",EDGE,"E5");var subQ4=makeQuery(id+"F3.opExtrude","SWEPT_FACE",FACE,{"disambiguationData":[OSD([subQ1])]});var subQ9=makeQuery(id+"F7.opPattern","COPY",EDGE,{"derivedFrom":makeQuery(id+"F2.opRevolve","SWEPT_EDGE",EDGE,{"disambiguationData":[OSD([subQ2,subQ1,subQ0])]}),"instanceName":"1"});var subQ10=makeQuery(id+"F1.opExtrude","SWEPT_FACE",FACE,{"disambiguationData":[OSD([subQ1])]});Q0=makeQuery(id+"F26.boolean.opBoolean","MERGE",EDGE,{"derivedFrom":[makeQuery(id+"F16.boolean.opBoolean","SPLIT",EDGE,{"disambiguationData":[TD([subQ10])],"derivedFrom":subQ9}),makeQuery(id+"F16.boolean.opBoolean","SPLIT",EDGE,{"disambiguationData":[TD([makeQuery(id+"F16.opExtrude","SWEPT_FACE",FACE,{"disambiguationData":[OSD([sQuery(id+"F14.wireOp",EDGE,"E36.MirrorCS")])]})])],"derivedFrom":subQ9}),makeQuery(id+"F16.boolean.opBoolean","SPLIT",EDGE,{"disambiguationData":[TD([makeQuery(id+"F16.opExtrude","SWEPT_FACE",FACE,{"disambiguationData":[OSD([sQuery(id+"F14.wireOp",EDGE,"E56.MirrorCS")])]})])],"derivedFrom":subQ9}),makeQuery(id+"F16.boolean.opBoolean","SPLIT",EDGE,{"disambiguationData":[TD([makeQuery(id+"F16.opExtrude","SWEPT_FACE",FACE,{"disambiguationData":[OSD([sQuery(id+"F14.wireOp",EDGE,"E40.MirrorCS")])]})])],"derivedFrom":subQ9}),makeQuery(id+"F16.boolean.opBoolean","SPLIT",EDGE,{"disambiguationData":[TD([subQ4])],"derivedFrom":subQ9}),makeQuery(id+"F26.opRevolve","SWEPT_EDGE",EDGE,{"disambiguationData":[OSD([subQ2,subQ1,subQ0])]})]});}
            var Q1;
            {var subQ0=sQuery(id+"F0.wireOp",EDGE,"E8");var subQ1=sQuery(id+"F0.wireOp",EDGE,"E6");var subQ2=makeQuery(id+"F3.opExtrude","SWEPT_EDGE",EDGE,{"disambiguationData":[OSD([sQuery(id+"F0.wireOp",EDGE,"E5"),subQ1,subQ0])]});Q1=makeQuery(id+"FmzSy8yVIfiXDki_2.boolean.opBoolean","MERGE",EDGE,{"derivedFrom":[makeQuery(id+"F7.boolean.opBoolean","MERGE",EDGE,{"derivedFrom":[subQ2,makeQuery(id+"F7.opPattern","COPY",EDGE,{"derivedFrom":subQ2,"instanceName":"1"})]}),makeQuery(id+"FmzSy8yVIfiXDki_2.opExtrude","SWEPT_EDGE",EDGE,{"disambiguationData":[OSD([subQ1,subQ0,sQuery(id+"F23.wireOp",EDGE,"E106")])]})]});}
            var Q2;
            {var subQ0=sQuery(id+"F0.wireOp",EDGE,"E8");var subQ1=sQuery(id+"F0.wireOp",EDGE,"E6");var subQ2=sQuery(id+"F0.wireOp",EDGE,"E5");var subQ8=makeQuery(id+"F2.opRevolve","SWEPT_EDGE",EDGE,{"disambiguationData":[OSD([subQ2,subQ1,subQ0])]});var subQ9=makeQuery(id+"F3.opExtrude","SWEPT_FACE",FACE,{"disambiguationData":[OSD([subQ1])]});var subQ10=makeQuery(id+"F1.opExtrude","SWEPT_FACE",FACE,{"disambiguationData":[OSD([subQ1])]});Q2=makeQuery(id+"F24.boolean.opBoolean","MERGE",EDGE,{"derivedFrom":[makeQuery(id+"F16.boolean.opBoolean","SPLIT",EDGE,{"disambiguationData":[TD([subQ10])],"derivedFrom":subQ8}),makeQuery(id+"F16.boolean.opBoolean","SPLIT",EDGE,{"disambiguationData":[TD([subQ9])],"derivedFrom":subQ8}),makeQuery(id+"F16.boolean.opBoolean","SPLIT",EDGE,{"disambiguationData":[TD([makeQuery(id+"F16.opExtrude","SWEPT_FACE",FACE,{"disambiguationData":[OSD([sQuery(id+"F14.wireOp",EDGE,"E42.MirrorCS")])]})])],"derivedFrom":subQ8}),makeQuery(id+"F16.boolean.opBoolean","SPLIT",EDGE,{"disambiguationData":[TD([makeQuery(id+"F16.opExtrude","SWEPT_FACE",FACE,{"disambiguationData":[OSD([sQuery(id+"F14.wireOp",EDGE,"E53.MirrorCS")])]})])],"derivedFrom":subQ8}),makeQuery(id+"F16.boolean.opBoolean","SPLIT",EDGE,{"disambiguationData":[TD([makeQuery(id+"F16.opExtrude","SWEPT_FACE",FACE,{"disambiguationData":[OSD([sQuery(id+"F14.wireOp",EDGE,"E47.MirrorCS")])]})])],"derivedFrom":subQ8}),makeQuery(id+"F24.opRevolve","SWEPT_EDGE",EDGE,{"disambiguationData":[OSD([subQ2,subQ1,subQ0])]})]});}
            fillet(context, id + "F31", {"entities" : qUnion([Q0, Q1, Q2]), "radius" : 2 * mm, "tangentPropagation" : true, "allowEdgeOverflow" : false});
        }
    });
